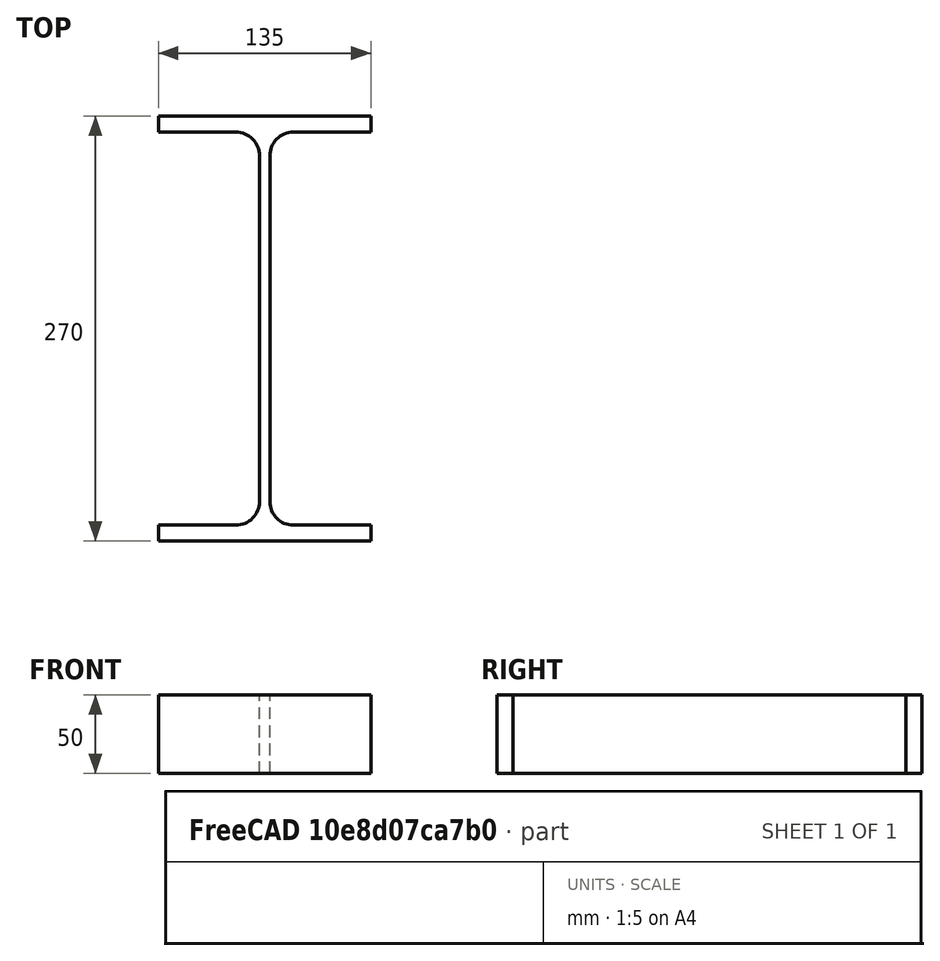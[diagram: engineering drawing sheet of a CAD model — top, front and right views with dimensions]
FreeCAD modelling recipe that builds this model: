
FCSTD DOCUMENT  (FreeCAD 0.15R4671 (Git))
Label: IPE-Profile 270 DIN1025-5 S235JR
License: All rights reserved
LicenseURL: http://en.wikipedia.org/wiki/All_rights_reserved
objects: Sketcher::SketchObject×1, Part::Extrusion×1
note: 2 computed .brp shape members not serialized (recipe doc carries the construction recipe); baked Part::Feature solids carry a one-line shape summary decoded from their .brp

FEATURE [Sketcher::SketchObject] Sketch
  sketch-geometry (16):
    g0: LineSegment StartX=3.3 StartY=-109.8 StartZ=0 EndX=3.3 EndY=109.8 EndZ=0
    g1: LineSegment StartX=18.3 StartY=124.8 StartZ=0 EndX=67.5 EndY=124.8 EndZ=0
    g2: LineSegment StartX=67.5 StartY=124.8 StartZ=0 EndX=67.5 EndY=135 EndZ=0
    g3: LineSegment StartX=67.5 StartY=135 StartZ=0 EndX=-67.5 EndY=135 EndZ=0
    g4: LineSegment StartX=-67.5 StartY=135 StartZ=0 EndX=-67.5 EndY=124.8 EndZ=0
    g5: LineSegment StartX=-67.5 StartY=124.8 StartZ=0 EndX=-18.3 EndY=124.8 EndZ=0
    g6: LineSegment StartX=-3.3 StartY=109.8 StartZ=0 EndX=-3.3 EndY=-109.8 EndZ=0
    g7: LineSegment StartX=-18.3 StartY=-124.8 StartZ=0 EndX=-67.5 EndY=-124.8 EndZ=0
    g8: LineSegment StartX=-67.5 StartY=-124.8 StartZ=0 EndX=-67.5 EndY=-135 EndZ=0
    g9: LineSegment StartX=-67.5 StartY=-135 StartZ=0 EndX=67.5 EndY=-135 EndZ=0
    g10: LineSegment StartX=67.5 StartY=-135 StartZ=0 EndX=67.5 EndY=-124.8 EndZ=0
    g11: LineSegment StartX=67.5 StartY=-124.8 StartZ=0 EndX=18.3 EndY=-124.8 EndZ=0
    g12: ArcOfCircle CenterX=18.3 CenterY=109.8 CenterZ=0 NormalX=0 NormalY=0 NormalZ=1 Radius=15 StartAngle=1.5708 EndAngle=3.14159
    g13: ArcOfCircle CenterX=18.3 CenterY=-109.8 CenterZ=0 NormalX=0 NormalY=0 NormalZ=1 Radius=15 StartAngle=3.14159 EndAngle=4.71239
    g14: ArcOfCircle CenterX=-18.3 CenterY=109.8 CenterZ=0 NormalX=0 NormalY=0 NormalZ=1 Radius=15 StartAngle=0 EndAngle=1.5708
    g15: ArcOfCircle CenterX=-18.3 CenterY=-109.8 CenterZ=0 NormalX=0 NormalY=0 NormalZ=1 Radius=15 StartAngle=4.71239 EndAngle=6.28319
  constraints (42):
    c: Vertical(g0)
    c: Coincident(g2,g1)
    c: Vertical(g2)
    c: Coincident(g3,g2)
    c: Coincident(g4,g3)
    c: Vertical(g4)
    c: Coincident(g5,g4)
    c: Horizontal(g5)
    c: Vertical(g6)
    c: Horizontal(g7)
    c: Coincident(g8,g7)
    c: Vertical(g8)
    c: Coincident(g9,g8)
    c: Horizontal(g9)
    c: Coincident(g10,g9)
    c: Vertical(g10)
    c: Coincident(g11,g10)
    c: Horizontal(g11)
    c: Tangent(g1,g12) = 1.5708
    c: Tangent(g0,g12) = 1.5708
    c: Tangent(g0,g13) = 1.5708
    c: Tangent(g11,g13) = 1.5708
    c: Tangent(g5,g14) = 1.5708
    c: Tangent(g6,g14) = 1.5708
    c: Tangent(g6,g15) = 1.5708
    c: Tangent(g7,g15) = 1.5708
    c: Equal(g3,g9)
    c: Equal(g2,g4)
    c: Equal(g4,g8)
    c: Equal(g8,g10)
    c: Equal(g12,g14)
    c: Equal(g14,g15)
    c: Equal(g15,g13)
    c: Symmetric(g2,g3,g-2)
    c: Symmetric(g9,g8,g-2)
    c: Symmetric(g0,g6,g-2)
    c: Symmetric(g2,g9,g-1)
    c: DistanceY(g2,g9) = -270
    c: DistanceX(g3) = -135
    c: DistanceX(g0,g6) = -6.6
    c: DistanceY(g2) = 10.2
    c: Radius(g12) = 15
FEATURE [Part::Extrusion] Extrude  label="IPE-Profile 270 DIN1025-5 S235JR"
  Base = -> Sketch
  Dir = (0,0,50)
  Solid = true
